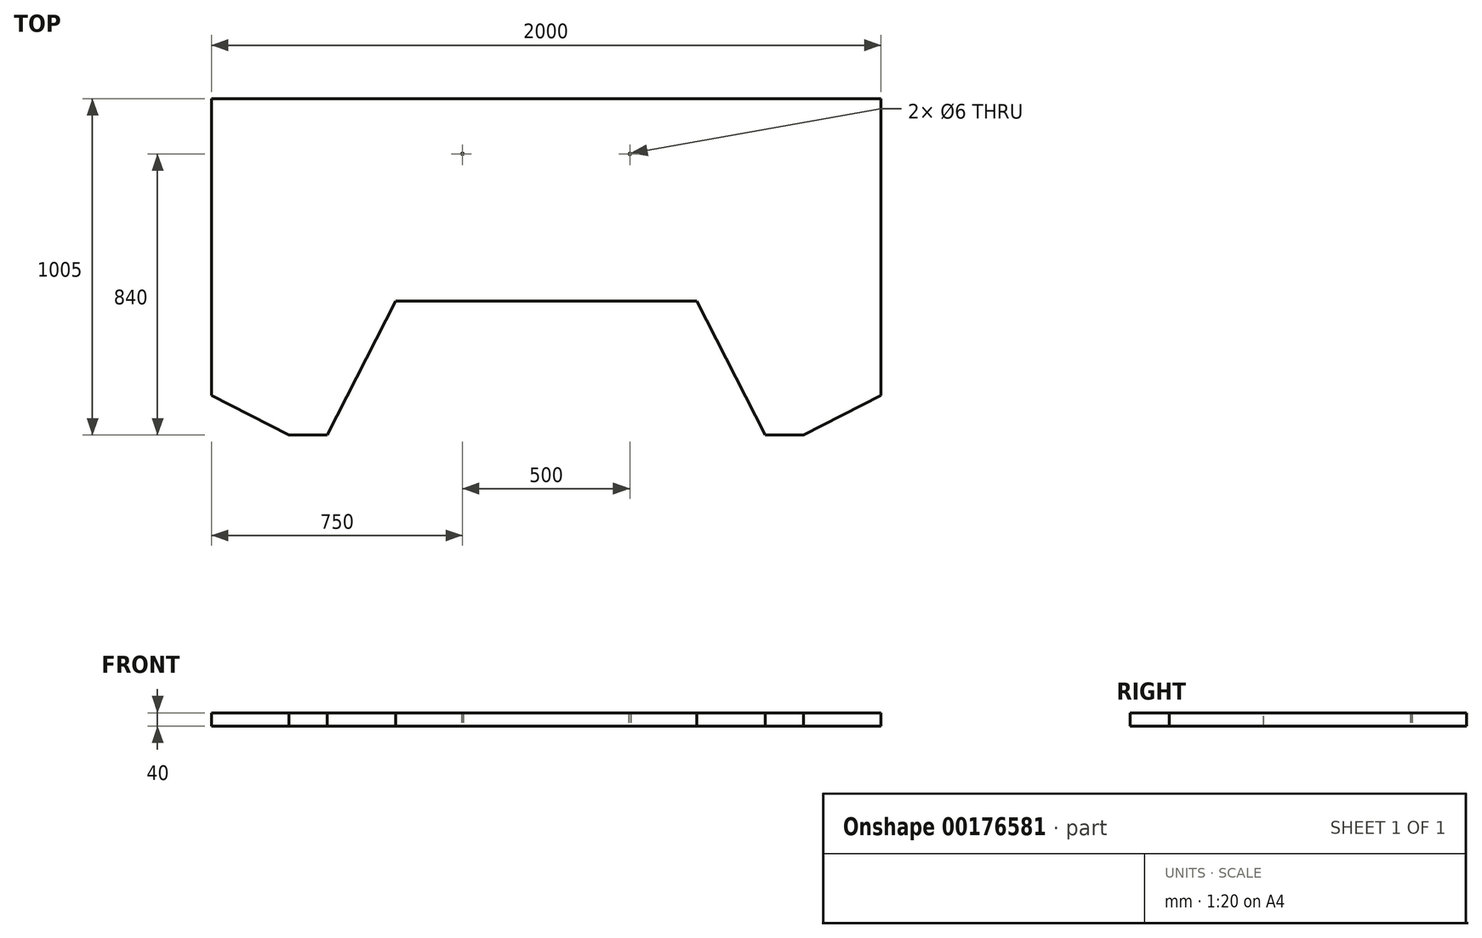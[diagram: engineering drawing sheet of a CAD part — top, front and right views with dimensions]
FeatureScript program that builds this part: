
annotation { "Feature Type Name" : "Feature", "Feature Type Description" : "" }
export const myFeature = defineFeature(function(context is Context, id is Id, definition is map)
    precondition{}
    {
        {
            var Q0;
            Q0=qCreatedBy(makeId("Top.planeOp"),FACE);
            var sketch = newSketch(context, id + "F0", { "sketchPlane" : qUnion([Q0])});
            skLineSegment(sketch, "E0.bottom", {"start": v(1000, -502.5) * mm, "end": v(-1000, -502.5) * mm});
            skLineSegment(sketch, "E0.top", {"start": v(1000, 502.5) * mm, "end": v(-1000, 502.5) * mm});
            skLineSegment(sketch, "E0.left", {"start": v(1000, -502.5) * mm, "end": v(1000, 502.5) * mm});
            skLineSegment(sketch, "E0.right", {"start": v(-1000, -502.5) * mm, "end": v(-1000, 502.5) * mm});
            skPoint(sketch, "E0.middle", {"position": v(0, 0) * mm});
            skSolve(sketch);
        }
        {
            var Q0;
            Q0 = qSketchRegion(id + "F0", true);
            extrude(context, id + "F1", {"entities" : qUnion([Q0]), "depth" : 40 * mm});
        }
        {
            var Q0;
            Q0=makeQuery(id+"F1.opExtrude","CAP_FACE",FACE,{"disambiguationData":[OSD([sQuery(id+"F0.wireOp",EDGE,"E0.bottom"),sQuery(id+"F0.wireOp",EDGE,"E0.top"),sQuery(id+"F0.wireOp",EDGE,"E0.left"),sQuery(id+"F0.wireOp",EDGE,"E0.right")])],"isStart":false});
            var sketch = newSketch(context, id + "F2", { "sketchPlane" : qUnion([Q0])});
            skLineSegment(sketch, "E1", {"start": v(0, 502.5) * mm, "end": v(0, -502.5) * mm, "construction": true});
            skLineSegment(sketch, "E2", {"start": v(-653.81, -502.5) * mm, "end": v(-450, -102.5) * mm});
            skLineSegment(sketch, "E3", {"start": v(-450, -102.5) * mm, "end": v(0, -102.5) * mm});
            skLineSegment(sketch, "E4.MirrorCS", {"start": v(450, -102.5) * mm, "end": v(0, -102.5) * mm});
            skLineSegment(sketch, "E5.MirrorCS", {"start": v(653.81, -502.5) * mm, "end": v(450, -102.5) * mm});
            skLineSegment(sketch, "E6", {"start": v(-653.81, -502.5) * mm, "end": v(0, -502.5) * mm});
            skLineSegment(sketch, "E7.MirrorCS", {"start": v(653.81, -502.5) * mm, "end": v(0, -502.5) * mm});
            skSolve(sketch);
        }
        {
            var Q0;
            Q0 = qSketchRegion(id + "F2", true);
            extrude(context, id + "F3", {"entities" : qUnion([Q0]), "operationType" : NewBodyOperationType.REMOVE, "endBound" : BoundingType.THROUGH_ALL, "oppositeDirection" : true, "depth" : 25 * mm});
        }
        {
            var Q0;
            Q0=makeQuery(id+"F1.opExtrude","CAP_FACE",FACE,{"disambiguationData":[OSD([sQuery(id+"F0.wireOp",EDGE,"E0.bottom"),sQuery(id+"F0.wireOp",EDGE,"E0.top"),sQuery(id+"F0.wireOp",EDGE,"E0.left"),sQuery(id+"F0.wireOp",EDGE,"E0.right")])],"isStart":false});
            var sketch = newSketch(context, id + "F4", { "sketchPlane" : qUnion([Q0])});
            skLineSegment(sketch, "E8.bottom", {"start": v(-1000, -502.5) * mm, "end": v(1000, -502.5) * mm});
            skLineSegment(sketch, "E8.left", {"start": v(-1000, -502.5) * mm, "end": v(-1000, 502.5) * mm});
            skLineSegment(sketch, "E8.right", {"start": v(1000, -502.5) * mm, "end": v(1000, 502.5) * mm});
            skLineSegment(sketch, "E9", {"start": v(-1000, 502.5) * mm, "end": v(-999, 502.5) * mm});
            skLineSegment(sketch, "E10", {"start": v(-999, 502.5) * mm, "end": v(-999, -501.5) * mm});
            skLineSegment(sketch, "E11", {"start": v(-999, -501.5) * mm, "end": v(0, -501.5) * mm});
            skPoint(sketch, "E11.endSnap0", {"position": v(0, -102.5) * mm});
            skLineSegment(sketch, "E12", {"start": v(0, 502.5) * mm, "end": v(0, 255.58) * mm, "construction": true});
            skLineSegment(sketch, "E13.MirrorCS", {"start": v(999, -501.5) * mm, "end": v(0, -501.5) * mm});
            skLineSegment(sketch, "E14.MirrorCS", {"start": v(999, 502.5) * mm, "end": v(999, -501.5) * mm});
            skLineSegment(sketch, "E15.MirrorCS", {"start": v(1000, 502.5) * mm, "end": v(999, 502.5) * mm});
            skSolve(sketch);
        }
        {
            var Q0;
            Q0=makeQuery(id+"F1.opExtrude","CAP_FACE",FACE,{"disambiguationData":[OSD([sQuery(id+"F0.wireOp",EDGE,"E0.bottom"),sQuery(id+"F0.wireOp",EDGE,"E0.top"),sQuery(id+"F0.wireOp",EDGE,"E0.left"),sQuery(id+"F0.wireOp",EDGE,"E0.right")])],"isStart":true});
            var sketch = newSketch(context, id + "F5", { "sketchPlane" : qUnion([Q0])});
            skLineSegment(sketch, "E16", {"start": v(0, -502.5) * mm, "end": v(0, -344.33) * mm, "construction": true});
            skPoint(sketch, "E16.endSnap0", {"position": v(0, -502.5) * mm});
            skCircle(sketch, "E17", {"center": v(-250, -337.5) * mm, "radius": 3 * mm});
            skCircle(sketch, "E18.MirrorC", {"center": v(250, -337.5) * mm, "radius": 3 * mm});
            skSolve(sketch);
        }
        {
            var Q0;
            Q0 = qSketchRegion(id + "F5", true);
            extrude(context, id + "F6", {"entities" : qUnion([Q0]), "operationType" : NewBodyOperationType.REMOVE, "endBound" : BoundingType.THROUGH_ALL, "oppositeDirection" : true, "depth" : 25 * mm});
        }
        {
            var Q0;
            Q0=makeQuery(id+"F1.opExtrude","CAP_FACE",FACE,{"disambiguationData":[OSD([sQuery(id+"F0.wireOp",EDGE,"E0.bottom"),sQuery(id+"F0.wireOp",EDGE,"E0.top"),sQuery(id+"F0.wireOp",EDGE,"E0.left"),sQuery(id+"F0.wireOp",EDGE,"E0.right")])],"isStart":false});
            var sketch = newSketch(context, id + "F7", { "sketchPlane" : qUnion([Q0])});
            skLineSegment(sketch, "E19", {"start": v(-1000, -384.5) * mm, "end": v(-768.41, -502.5) * mm});
            skLineSegment(sketch, "E20", {"start": v(-768.41, -502.5) * mm, "end": v(-1000, -502.5) * mm});
            skLineSegment(sketch, "E21", {"start": v(-1000, -502.5) * mm, "end": v(-1000, -384.5) * mm});
            skLineSegment(sketch, "E22", {"start": v(0, -102.5) * mm, "end": v(0, 139.59) * mm, "construction": true});
            skPoint(sketch, "E22.endSnap0", {"position": v(0, -102.5) * mm});
            skLineSegment(sketch, "E23.MirrorCS", {"start": v(1000, -384.5) * mm, "end": v(768.41, -502.5) * mm});
            skLineSegment(sketch, "E24.MirrorCS", {"start": v(768.41, -502.5) * mm, "end": v(1000, -502.5) * mm});
            skLineSegment(sketch, "E25.MirrorCS", {"start": v(1000, -502.5) * mm, "end": v(1000, -384.5) * mm});
            skSolve(sketch);
        }
        {
            var Q0;
            Q0 = qSketchRegion(id + "F7", true);
            extrude(context, id + "F8", {"entities" : qUnion([Q0]), "operationType" : NewBodyOperationType.REMOVE, "endBound" : BoundingType.THROUGH_ALL, "oppositeDirection" : true, "depth" : 25 * mm});
        }
    });
